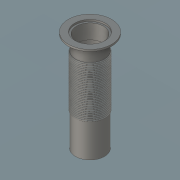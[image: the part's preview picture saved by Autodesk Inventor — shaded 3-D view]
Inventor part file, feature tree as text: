
AUTODESK INVENTOR PART (.ipt)
format: ipt  version: 2018 (Build 220112000, 112)  size: 308,736 bytes
history: native  units: in
note: dims shown in document units (in); Inventor stores cm internally (conversion verified against a paired STEP export)
features: sketch x6, extrude x5, revolve x1
ambient origin geometry x8: Origin, YZ Plane, XZ Plane, XY Plane, X Axis, Y Axis, Z Axis, Center Point
bodies: Solid1 (feature_tree)
feature tree (12):
  extrude  "Extrusion1"  Depth=2.07in
  extrude  "Extrusion2"  Depth=0.12in
  extrude  "Extrusion3"  Depth=0.12in TaperAngle=0.0deg
  extrude  "Extrusion4"  Depth=1.0in TaperAngle=0.0deg
  revolve  "Revolution1"  [1 undecoded]
  extrude  "Extrusion5"  Depth=3.5in
  sketch  "Sketch1"  dims[d0=2.95in d1=2.07in]
  sketch  "Sketch2"  dims[d2=0.12in d3=0.0in d4=0.25in d5=-0.5154in]
  sketch  "Sketch3"  dims[d6=0.12in d7=0.25in d8=0.0in]
  sketch  "Sketch4"  dims[d9=1.97in d10=1.0in d11=0.0in]
  sketch  "Sketch5"  dims[d12=0.05in d15=13.7795in d17=0.1in d18=0.3937in d20=1.0in]
  sketch  "Sketch6"  dims[d22=0.06in d23=3.5in d24=90.0deg d25=2.25in d26=0.0in]
note: 1 required parameter value undecoded (feature->parameter linkage not recoverable at this tier; creation-order binding heuristic only, values carry confidence <= 0.55)
